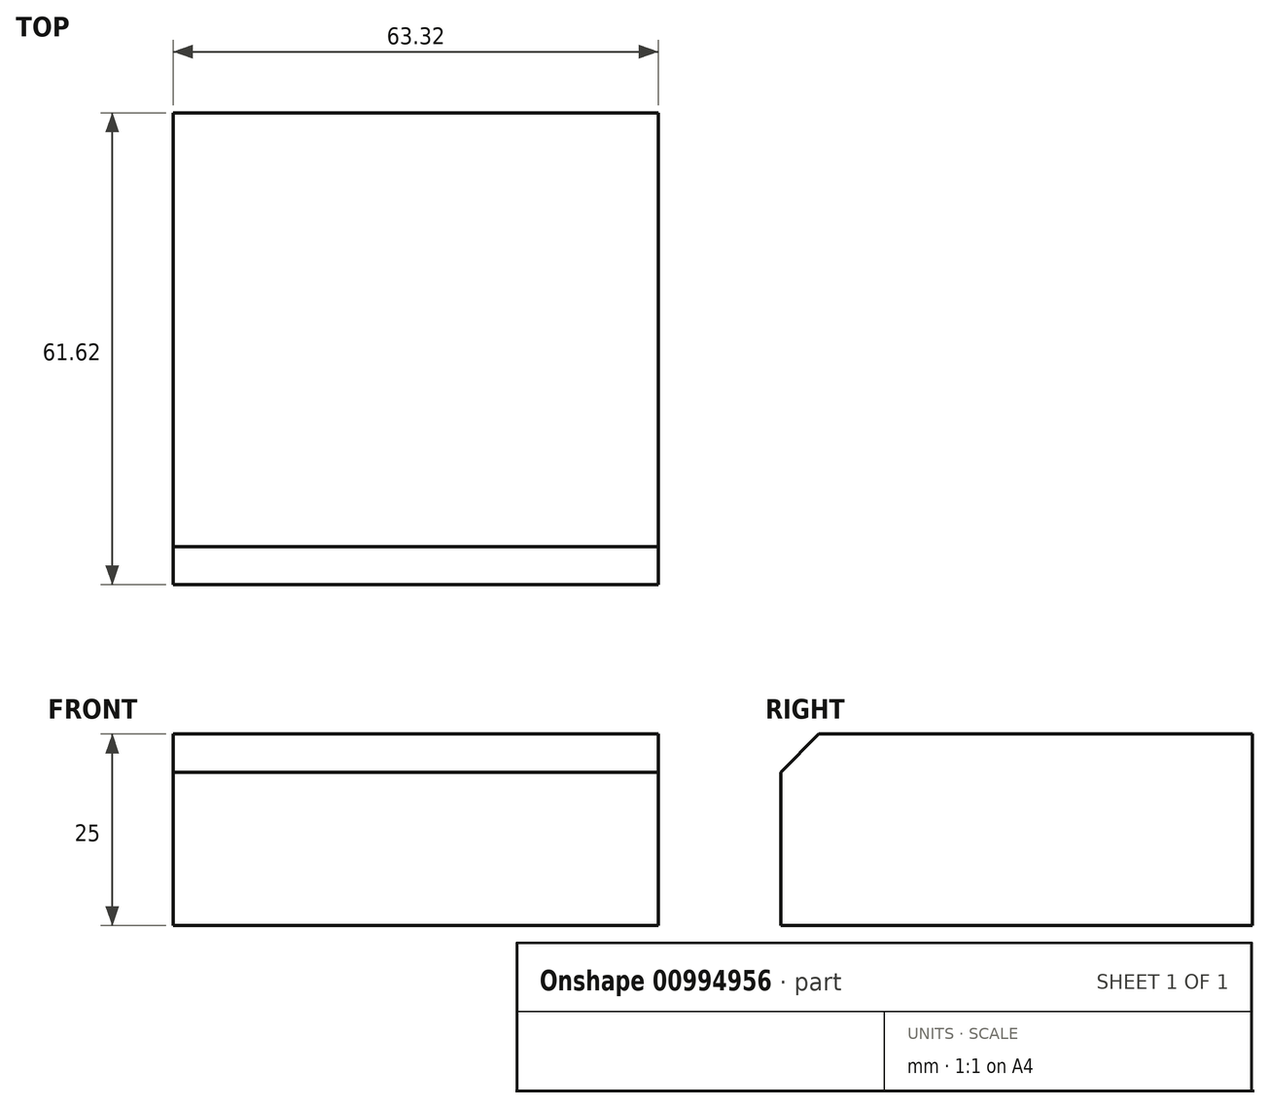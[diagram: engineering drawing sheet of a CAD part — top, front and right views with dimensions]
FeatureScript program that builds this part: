
annotation { "Feature Type Name" : "Feature", "Feature Type Description" : "" }
export const myFeature = defineFeature(function(context is Context, id is Id, definition is map)
    precondition{}
    {
        {
            var Q0;
            Q0=qCreatedBy(makeId("Top.planeOp"),FACE);
            var sketch = newSketch(context, id + "F0", { "sketchPlane" : qUnion([Q0])});
            skLineSegment(sketch, "E0.bottom", {"start": v(31.66, -30.8) * mm, "end": v(-31.66, -30.8) * mm});
            skLineSegment(sketch, "E0.top", {"start": v(31.66, 30.8) * mm, "end": v(-31.66, 30.8) * mm});
            skLineSegment(sketch, "E0.left", {"start": v(31.66, -30.8) * mm, "end": v(31.66, 30.8) * mm});
            skLineSegment(sketch, "E0.right", {"start": v(-31.66, -30.8) * mm, "end": v(-31.66, 30.8) * mm});
            skPoint(sketch, "E0.middle", {"position": v(0, 0) * mm});
            skSolve(sketch);
        }
        {
            var Q0;
            Q0=qSketchRegion(id+"F0",true);
            extrude(context, id + "F1", {"entities" : qUnion([Q0]), "depth" : 25 * mm, "offsetDistance" : 25 * mm});
        }
        {
            var Q0;
            Q0=makeQuery(id+"F1.opExtrude","CAP_EDGE",EDGE,{"disambiguationData":[OSD([sQuery(id+"F0.wireOp",EDGE,"E0.bottom")])],"isStart":false});
            chamfer(context, id + "F2", {"entities" : qUnion([Q0]), "width" : 5 * mm, "tangentPropagation" : true});
        }
    });
